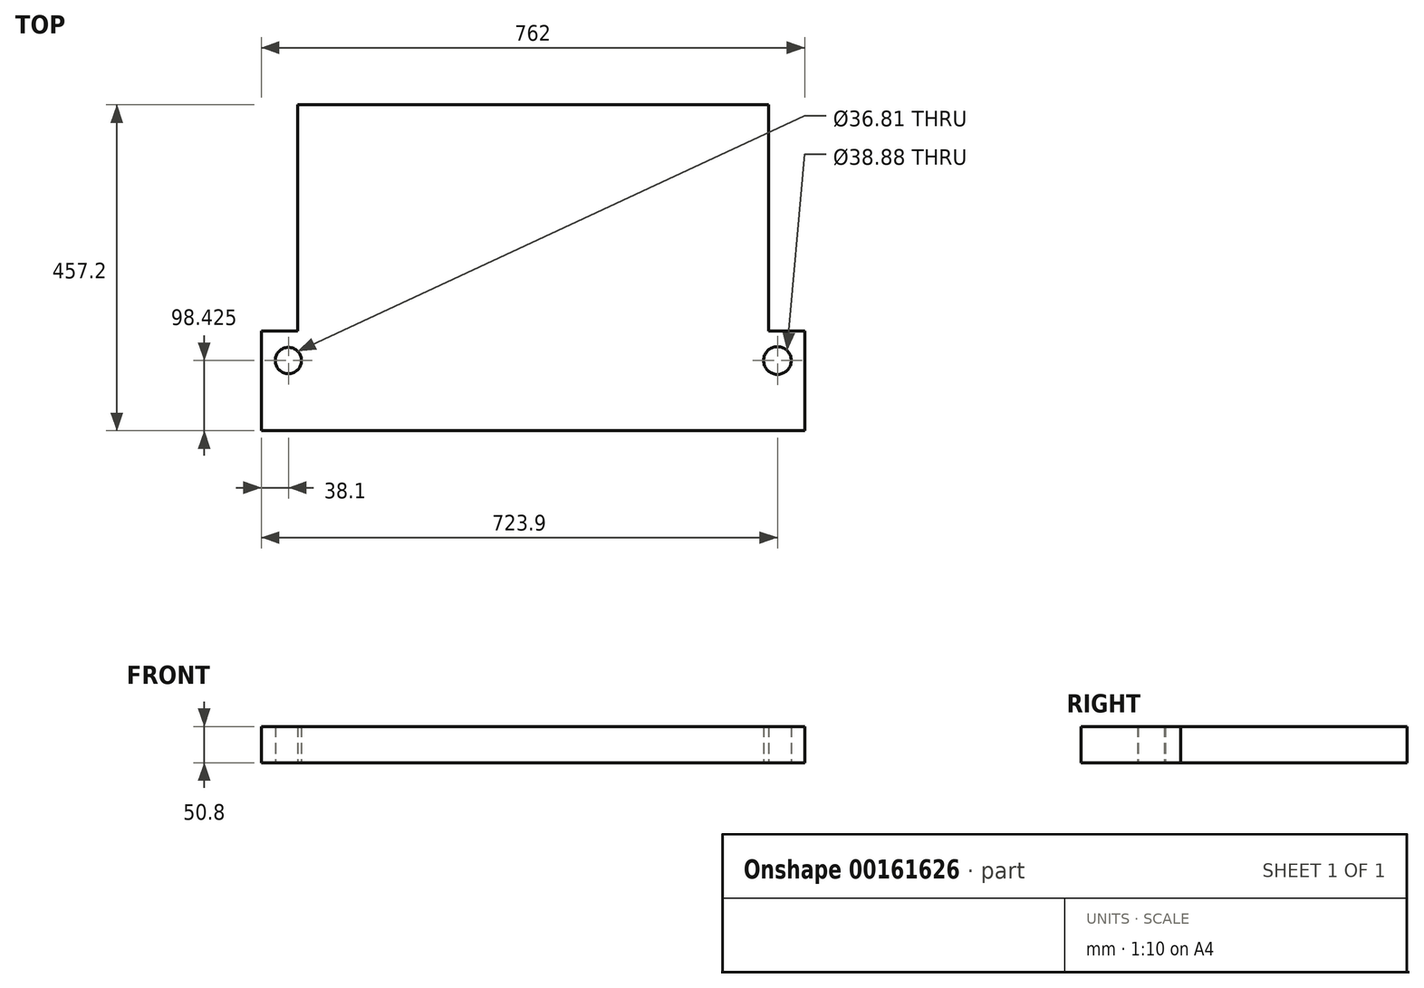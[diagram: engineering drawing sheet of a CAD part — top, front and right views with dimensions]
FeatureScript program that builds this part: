
annotation { "Feature Type Name" : "Feature", "Feature Type Description" : "" }
export const myFeature = defineFeature(function(context is Context, id is Id, definition is map)
    precondition{}
    {
        {
            var Q0;
            Q0=qCreatedBy(makeId("Top.planeOp"),FACE);
            var sketch = newSketch(context, id + "F0", { "sketchPlane" : qUnion([Q0])});
            skLineSegment(sketch, "E0.bottom", {"start": v(330.2, 228.6) * mm, "end": v(-330.2, 228.6) * mm});
            skLineSegment(sketch, "E0.top", {"start": v(381, -228.6) * mm, "end": v(-381, -228.6) * mm});
            skLineSegment(sketch, "E0.left", {"start": v(381, -88.9) * mm, "end": v(381, -228.6) * mm});
            skLineSegment(sketch, "E0.right", {"start": v(-381, -88.9) * mm, "end": v(-381, -228.6) * mm});
            skPoint(sketch, "E0.middle", {"position": v(0, 0) * mm});
            skLineSegment(sketch, "E1.top", {"start": v(-381, -88.9) * mm, "end": v(-330.2, -88.9) * mm});
            skLineSegment(sketch, "E1.right", {"start": v(-330.2, 228.6) * mm, "end": v(-330.2, -88.9) * mm});
            skLineSegment(sketch, "E2.top", {"start": v(381, -88.9) * mm, "end": v(330.2, -88.9) * mm});
            skLineSegment(sketch, "E2.right", {"start": v(330.2, 228.6) * mm, "end": v(330.2, -88.9) * mm});
            skCircle(sketch, "E3", {"center": v(-342.9, -130.18) * mm, "radius": 18.4 * mm});
            skCircle(sketch, "E4", {"center": v(342.9, -130.17) * mm, "radius": 19.44 * mm});
            skSolve(sketch);
        }
        {
            var Q0;
            Q0=makeQuery(id+"F0.imprint","IMPRINT",FACE,{"disambiguationData":[TD([[makeQuery(id+"F0.imprint","IMPRINT",EDGE,{"derivedFrom":sQuery(id+"F0.wireOp",EDGE,"E0.bottom")}),1.0]])]});
            extrude(context, id + "F1", {"entities" : qUnion([Q0]), "depth" : 50.8 * mm});
        }
    });
